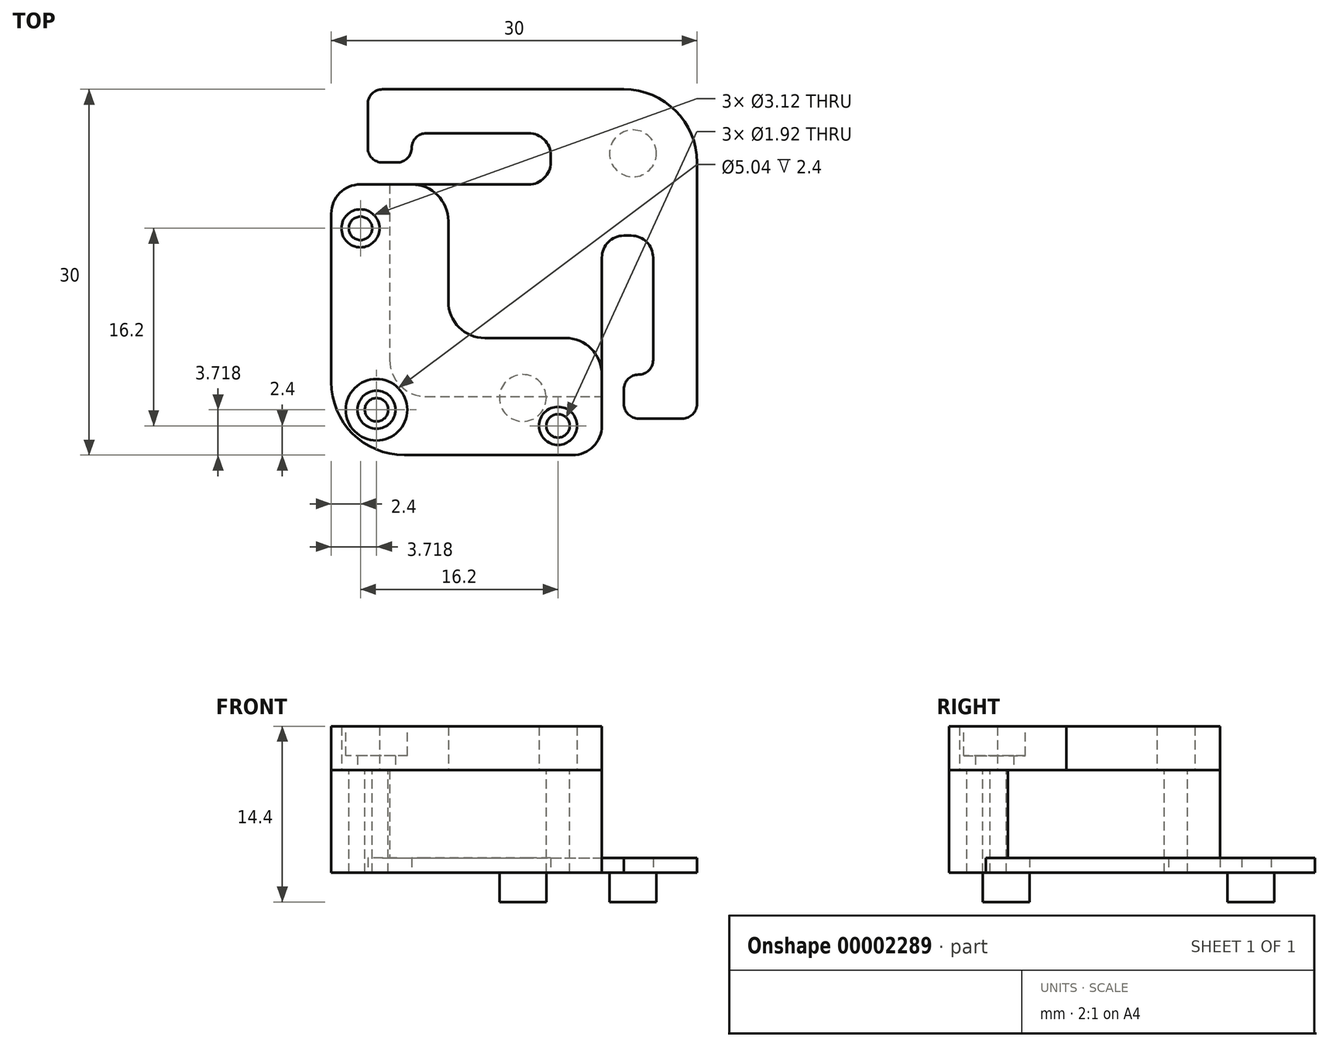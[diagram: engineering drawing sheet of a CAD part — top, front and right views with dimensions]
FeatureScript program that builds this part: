
annotation { "Feature Type Name" : "Feature", "Feature Type Description" : "" }
export const myFeature = defineFeature(function(context is Context, id is Id, definition is map)
    precondition{}
    {
        {
            var Q0;
            Q0=qCreatedBy(makeId("Top.planeOp"),FACE);
            var sketch = newSketch(context, id + "F0", { "sketchPlane" : qUnion([Q0])});
            skLineSegment(sketch, "E0.top", {"start": v(3.5, 25) * mm, "end": v(20, 25) * mm});
            skLineSegment(sketch, "E0.left", {"start": v(0, 5) * mm, "end": v(0, 16.5) * mm});
            skLineSegment(sketch, "E1", {"start": v(13.5, 22) * mm, "end": v(6.5, 22) * mm});
            skLineSegment(sketch, "E2", {"start": v(2, 18.5) * mm, "end": v(13.5, 18.5) * mm});
            skLineSegment(sketch, "E3", {"start": v(15, 20.5) * mm, "end": v(15, 20) * mm});
            skArc(sketch, "E4.filletArc", {"start": v(15, 20.5) * mm, "mid": v(14.56, 21.56) * mm, "end": v(13.5, 22) * mm});
            skArc(sketch, "E5.filletArc", {"start": v(13.5, 18.5) * mm, "mid": v(14.56, 18.94) * mm, "end": v(15, 20) * mm});
            skArc(sketch, "E6.filletArc", {"start": v(2, 18.5) * mm, "mid": v(0.59, 17.91) * mm, "end": v(0, 16.5) * mm});
            skPoint(sketch, "E7.visualSharp", {"position": v(0, 0) * mm});
            skLineSegment(sketch, "E8", {"start": v(5.5, 21) * mm, "end": v(5.5, 21) * mm});
            skLineSegment(sketch, "E9", {"start": v(4.5, 20) * mm, "end": v(3.5, 20) * mm});
            skLineSegment(sketch, "E10", {"start": v(2.5, 21) * mm, "end": v(2.5, 24) * mm});
            skPoint(sketch, "E11.visualSharp", {"position": v(5.5, 20) * mm});
            skArc(sketch, "E11.filletArc", {"start": v(4.5, 20) * mm, "mid": v(5.2, 20.3) * mm, "end": v(5.5, 21) * mm});
            skArc(sketch, "E12.filletArc", {"start": v(2.5, 21) * mm, "mid": v(2.8, 20.3) * mm, "end": v(3.5, 20) * mm});
            skArc(sketch, "E13.filletArc", {"start": v(6.5, 22) * mm, "mid": v(5.8, 21.7) * mm, "end": v(5.5, 21) * mm});
            skPoint(sketch, "E14.visualSharp", {"position": v(2.5, 25) * mm});
            skArc(sketch, "E14.filletArc", {"start": v(3.5, 25) * mm, "mid": v(2.8, 24.7) * mm, "end": v(2.5, 24) * mm});
            skLineSegment(sketch, "E15.bottom", {"start": v(0, 0) * mm, "end": v(25, 0) * mm, "construction": true});
            skLineSegment(sketch, "E15.top", {"start": v(0, 25) * mm, "end": v(25, 25) * mm, "construction": true});
            skLineSegment(sketch, "E15.left", {"start": v(0, 0) * mm, "end": v(0, 25) * mm, "construction": true});
            skLineSegment(sketch, "E15.right", {"start": v(25, 0) * mm, "end": v(25, 25) * mm, "construction": true});
            skLineSegment(sketch, "E16", {"start": v(0, 0) * mm, "end": v(25, 25) * mm, "construction": true});
            skLineSegment(sketch, "E17.0.MirrorCS", {"start": v(5, 0) * mm, "end": v(16.5, 0) * mm});
            skArc(sketch, "E18.0.MirrorCS", {"start": v(18.5, 2) * mm, "mid": v(17.91, 0.59) * mm, "end": v(16.5, 0) * mm});
            skLineSegment(sketch, "E19.0.MirrorCS", {"start": v(18.5, 2) * mm, "end": v(18.5, 13.5) * mm});
            skArc(sketch, "E20.0.MirrorCS", {"start": v(18.5, 13.5) * mm, "mid": v(18.94, 14.56) * mm, "end": v(20, 15) * mm});
            skLineSegment(sketch, "E21.0.MirrorCS", {"start": v(20.5, 15) * mm, "end": v(20, 15) * mm});
            skArc(sketch, "E22.0.MirrorCS", {"start": v(20.5, 15) * mm, "mid": v(21.56, 14.56) * mm, "end": v(22, 13.5) * mm});
            skLineSegment(sketch, "E23.0.MirrorCS", {"start": v(22, 13.5) * mm, "end": v(22, 6.5) * mm});
            skArc(sketch, "E24.0.MirrorCS", {"start": v(22, 6.5) * mm, "mid": v(21.7, 5.8) * mm, "end": v(21, 5.5) * mm});
            skArc(sketch, "E25.0.MirrorCS", {"start": v(20, 4.5) * mm, "mid": v(20.3, 5.2) * mm, "end": v(21, 5.5) * mm});
            skLineSegment(sketch, "E26.0.MirrorCS", {"start": v(20, 4.5) * mm, "end": v(20, 3.5) * mm});
            skArc(sketch, "E27.0.MirrorCS", {"start": v(21, 2.5) * mm, "mid": v(20.3, 2.8) * mm, "end": v(20, 3.5) * mm});
            skLineSegment(sketch, "E28.0.MirrorCS", {"start": v(21, 2.5) * mm, "end": v(24, 2.5) * mm});
            skArc(sketch, "E29.0.MirrorCS", {"start": v(25, 3.5) * mm, "mid": v(24.7, 2.8) * mm, "end": v(24, 2.5) * mm});
            skLineSegment(sketch, "E30.0.MirrorCS", {"start": v(25, 3.5) * mm, "end": v(25, 20) * mm});
            skArc(sketch, "E31.filletArc", {"start": v(0, 5) * mm, "mid": v(1.46, 1.46) * mm, "end": v(5, 0) * mm});
            skPoint(sketch, "E32.visualSharp", {"position": v(25, 25) * mm});
            skArc(sketch, "E32.filletArc", {"start": v(25, 20) * mm, "mid": v(23.54, 23.54) * mm, "end": v(20, 25) * mm});
            skSolve(sketch);
        }
        {
            var Q0;
            Q0=makeQuery(id+"F0.imprint","IMPRINT",FACE,{"disambiguationData":[TD([[makeQuery(id+"F0.imprint","IMPRINT",EDGE,{"derivedFrom":sQuery(id+"F0.wireOp",EDGE,"E0.bottom")}),1.0]])]});
            var Q1;
            Q1=makeQuery(id+"F0.imprint","IMPRINT",FACE,{"disambiguationData":[TD([[makeQuery(id+"F0.imprint","IMPRINT",EDGE,{"derivedFrom":sQuery(id+"F0.wireOp",EDGE,"E0.top")}),-1.0]])]});
            extrude(context, id + "F1", {"entities" : qUnion([Q0, Q1]), "depth" : 3 * mm});
        }
        {
            var Q0;
            Q0=makeQuery(id+"F1.opExtrude","CAP_FACE",FACE,{"disambiguationData":[OSD([sQuery(id+"F0.wireOp",EDGE,"E0.top"),sQuery(id+"F0.wireOp",EDGE,"E0.left"),sQuery(id+"F0.wireOp",EDGE,"E1"),sQuery(id+"F0.wireOp",EDGE,"E2"),sQuery(id+"F0.wireOp",EDGE,"E3"),sQuery(id+"F0.wireOp",EDGE,"E4.filletArc"),sQuery(id+"F0.wireOp",EDGE,"E5.filletArc"),sQuery(id+"F0.wireOp",EDGE,"E6.filletArc"),sQuery(id+"F0.wireOp",EDGE,"E9"),sQuery(id+"F0.wireOp",EDGE,"E10"),sQuery(id+"F0.wireOp",EDGE,"E11.filletArc"),sQuery(id+"F0.wireOp",EDGE,"E12.filletArc"),sQuery(id+"F0.wireOp",EDGE,"E13.filletArc"),sQuery(id+"F0.wireOp",EDGE,"E14.filletArc"),sQuery(id+"F0.wireOp",EDGE,"E17.0.MirrorCS"),sQuery(id+"F0.wireOp",EDGE,"E18.0.MirrorCS"),sQuery(id+"F0.wireOp",EDGE,"E19.0.MirrorCS"),sQuery(id+"F0.wireOp",EDGE,"E20.0.MirrorCS"),sQuery(id+"F0.wireOp",EDGE,"E21.0.MirrorCS"),sQuery(id+"F0.wireOp",EDGE,"E22.0.MirrorCS"),sQuery(id+"F0.wireOp",EDGE,"E23.0.MirrorCS"),sQuery(id+"F0.wireOp",EDGE,"E24.0.MirrorCS"),sQuery(id+"F0.wireOp",EDGE,"E25.0.MirrorCS"),sQuery(id+"F0.wireOp",EDGE,"E26.0.MirrorCS"),sQuery(id+"F0.wireOp",EDGE,"E27.0.MirrorCS"),sQuery(id+"F0.wireOp",EDGE,"E28.0.MirrorCS"),sQuery(id+"F0.wireOp",EDGE,"E29.0.MirrorCS"),sQuery(id+"F0.wireOp",EDGE,"E30.0.MirrorCS"),sQuery(id+"F0.wireOp",EDGE,"E31.filletArc"),sQuery(id+"F0.wireOp",EDGE,"E32.filletArc")])],"isStart":false});
            var sketch = newSketch(context, id + "F2", { "sketchPlane" : qUnion([Q0])});
            skLineSegment(sketch, "E33", {"start": v(0, 16.5) * mm, "end": v(0, 5) * mm});
            skLineSegment(sketch, "E34", {"start": v(5, 0) * mm, "end": v(16.5, 0) * mm});
            skLineSegment(sketch, "E35", {"start": v(4, 18.5) * mm, "end": v(4, 6.5) * mm});
            skLineSegment(sketch, "E36", {"start": v(6.5, 4) * mm, "end": v(18.5, 4) * mm});
            skLineSegment(sketch, "E37", {"start": v(2, 18.5) * mm, "end": v(4, 18.5) * mm});
            skLineSegment(sketch, "E38", {"start": v(18.5, 4) * mm, "end": v(18.5, 2) * mm});
            skArc(sketch, "E39", {"start": v(0, 5) * mm, "mid": v(1.46, 1.46) * mm, "end": v(5, 0) * mm});
            skArc(sketch, "E40", {"start": v(16.5, 0) * mm, "mid": v(17.91, 0.59) * mm, "end": v(18.5, 2) * mm});
            skArc(sketch, "E41", {"start": v(2, 18.5) * mm, "mid": v(0.59, 17.91) * mm, "end": v(0, 16.5) * mm});
            skPoint(sketch, "E42.visualSharp", {"position": v(4, 4) * mm});
            skArc(sketch, "E42.filletArc", {"start": v(4, 6.5) * mm, "mid": v(4.73, 4.73) * mm, "end": v(6.5, 4) * mm});
            skSolve(sketch);
        }
        {
            var Q0;
            Q0=makeQuery(id+"F2.imprint","IMPRINT",FACE,{"disambiguationData":[TD([[makeQuery(id+"F2.imprint","IMPRINT",EDGE,{"derivedFrom":sQuery(id+"F2.wireOp",EDGE,"E33")}),-1.0]])]});
            extrude(context, id + "F3", {"entities" : qUnion([Q0]), "operationType" : NewBodyOperationType.ADD, "depth" : 6 * mm});
        }
        {
            var Q0;
            Q0=makeQuery(id+"F3.opExtrude","CAP_FACE",FACE,{"disambiguationData":[OSD([sQuery(id+"F2.wireOp",EDGE,"E33"),sQuery(id+"F2.wireOp",EDGE,"E34"),sQuery(id+"F2.wireOp",EDGE,"E35"),sQuery(id+"F2.wireOp",EDGE,"E36"),sQuery(id+"F2.wireOp",EDGE,"E37"),sQuery(id+"F2.wireOp",EDGE,"E38"),sQuery(id+"F2.wireOp",EDGE,"E39"),sQuery(id+"F2.wireOp",EDGE,"E40"),sQuery(id+"F2.wireOp",EDGE,"E41"),sQuery(id+"F2.wireOp",EDGE,"E42.filletArc")])],"isStart":false});
            var sketch = newSketch(context, id + "F4", { "sketchPlane" : qUnion([Q0])});
            skLineSegment(sketch, "E43", {"start": v(0, 5) * mm, "end": v(0, 16.5) * mm});
            skLineSegment(sketch, "E44", {"start": v(2, 18.5) * mm, "end": v(5.5, 18.5) * mm});
            skLineSegment(sketch, "E45", {"start": v(8, 16) * mm, "end": v(8, 10.5) * mm});
            skLineSegment(sketch, "E46", {"start": v(10.5, 8) * mm, "end": v(16, 8) * mm});
            skLineSegment(sketch, "E47", {"start": v(18.5, 5.5) * mm, "end": v(18.5, 2) * mm});
            skLineSegment(sketch, "E48", {"start": v(5, 0) * mm, "end": v(16.5, 0) * mm});
            skArc(sketch, "E49", {"start": v(2, 18.5) * mm, "mid": v(0.59, 17.91) * mm, "end": v(0, 16.5) * mm});
            skArc(sketch, "E50", {"start": v(0, 5) * mm, "mid": v(1.46, 1.46) * mm, "end": v(5, 0) * mm});
            skArc(sketch, "E51", {"start": v(16.5, 0) * mm, "mid": v(17.91, 0.59) * mm, "end": v(18.5, 2) * mm});
            skPoint(sketch, "E52.visualSharp", {"position": v(8, 8) * mm});
            skArc(sketch, "E52.filletArc", {"start": v(8, 10.5) * mm, "mid": v(8.73, 8.73) * mm, "end": v(10.5, 8) * mm});
            skPoint(sketch, "E53.visualSharp", {"position": v(8, 18.5) * mm});
            skArc(sketch, "E53.filletArc", {"start": v(8, 16) * mm, "mid": v(7.27, 17.77) * mm, "end": v(5.5, 18.5) * mm});
            skPoint(sketch, "E54.visualSharp", {"position": v(18.5, 8) * mm});
            skArc(sketch, "E54.filletArc", {"start": v(18.5, 5.5) * mm, "mid": v(17.77, 7.27) * mm, "end": v(16, 8) * mm});
            skSolve(sketch);
        }
        {
            var Q0;
            {var subQ10=sQuery(id+"F4.wireOp",EDGE,"E45");Q0=qUnion([makeQuery(id+"F4.imprint","IMPRINT",FACE,{"disambiguationData":[TD([[makeQuery(id+"F4.imprint","IMPRINT",EDGE,{"derivedFrom":subQ10}),-1.0]])]}),makeQuery(id+"F4.imprint","IMPRINT",FACE,{"disambiguationData":[TD([[makeQuery(id+"F4.imprint","IMPRINT",EDGE,{"derivedFrom":sQuery(id+"F4.wireOp",EDGE,"E43")}),-1.0]])]})]);}
            extrude(context, id + "F5", {"entities" : qUnion([Q0]), "depth" : 3 * mm});
        }
        {
            var Q0;
            Q0=makeQuery(id+"F3.opExtrude","CAP_FACE",FACE,{"disambiguationData":[OSD([sQuery(id+"F2.wireOp",EDGE,"E33"),sQuery(id+"F2.wireOp",EDGE,"E34"),sQuery(id+"F2.wireOp",EDGE,"E35"),sQuery(id+"F2.wireOp",EDGE,"E36"),sQuery(id+"F2.wireOp",EDGE,"E37"),sQuery(id+"F2.wireOp",EDGE,"E38"),sQuery(id+"F2.wireOp",EDGE,"E39"),sQuery(id+"F2.wireOp",EDGE,"E40"),sQuery(id+"F2.wireOp",EDGE,"E41"),sQuery(id+"F2.wireOp",EDGE,"E42.filletArc")])],"isStart":false});
            var sketch = newSketch(context, id + "F6", { "sketchPlane" : qUnion([Q0])});
            skLineSegment(sketch, "E55", {"start": v(2, 18.57) * mm, "end": v(2, 2) * mm, "construction": true});
            skLineSegment(sketch, "E56", {"start": v(2, 2) * mm, "end": v(18.57, 2) * mm, "construction": true});
            skCircle(sketch, "E57", {"center": v(2, 15.5) * mm, "radius": 0.8 * mm});
            skCircle(sketch, "E58", {"center": v(3.1, 3.1) * mm, "radius": 0.8 * mm});
            skCircle(sketch, "E59", {"center": v(15.5, 2) * mm, "radius": 0.8 * mm});
            skLineSegment(sketch, "E60", {"start": v(1.46, 1.46) * mm, "end": v(4.73, 4.73) * mm, "construction": true});
            skCircle(sketch, "E61", {"center": v(2, 15.5) * mm, "radius": 1.3 * mm});
            skCircle(sketch, "E62", {"center": v(3.1, 3.1) * mm, "radius": 1.3 * mm});
            skCircle(sketch, "E63", {"center": v(15.5, 2) * mm, "radius": 1.3 * mm});
            skSolve(sketch);
        }
        {
            var Q0;
            Q0=makeQuery(id+"F6.imprint","IMPRINT",FACE,{"disambiguationData":[TD([[makeQuery(id+"F6.imprint","IMPRINT",EDGE,{"derivedFrom":sQuery(id+"F6.wireOp",EDGE,"E58")}),1.0]])]});
            var Q1;
            Q1=makeQuery(id+"F6.imprint","IMPRINT",FACE,{"disambiguationData":[TD([[makeQuery(id+"F6.imprint","IMPRINT",EDGE,{"derivedFrom":sQuery(id+"F6.wireOp",EDGE,"E57")}),1.0]])]});
            var Q2;
            Q2=makeQuery(id+"F6.imprint","IMPRINT",FACE,{"disambiguationData":[TD([[makeQuery(id+"F6.imprint","IMPRINT",EDGE,{"derivedFrom":sQuery(id+"F6.wireOp",EDGE,"E59")}),1.0]])]});
            extrude(context, id + "F7", {"entities" : qUnion([Q0, Q1, Q2]), "operationType" : NewBodyOperationType.REMOVE, "oppositeDirection" : true, "depth" : 25 * mm});
        }
        {
            var Q0;
            Q0=makeQuery(id+"F6.imprint","IMPRINT",FACE,{"disambiguationData":[TD([[makeQuery(id+"F6.imprint","IMPRINT",EDGE,{"derivedFrom":sQuery(id+"F6.wireOp",EDGE,"E58")}),-1.0]])]});
            var Q1;
            Q1=makeQuery(id+"F6.imprint","IMPRINT",FACE,{"disambiguationData":[TD([[makeQuery(id+"F6.imprint","IMPRINT",EDGE,{"derivedFrom":sQuery(id+"F6.wireOp",EDGE,"E58")}),1.0]])]});
            var Q2;
            Q2=makeQuery(id+"F6.imprint","IMPRINT",FACE,{"disambiguationData":[TD([[makeQuery(id+"F6.imprint","IMPRINT",EDGE,{"derivedFrom":sQuery(id+"F6.wireOp",EDGE,"E57")}),1.0]])]});
            var Q3;
            Q3=makeQuery(id+"F6.imprint","IMPRINT",FACE,{"disambiguationData":[TD([[makeQuery(id+"F6.imprint","IMPRINT",EDGE,{"derivedFrom":sQuery(id+"F6.wireOp",EDGE,"E57")}),-1.0]])]});
            var Q4;
            Q4=makeQuery(id+"F6.imprint","IMPRINT",FACE,{"disambiguationData":[TD([[makeQuery(id+"F6.imprint","IMPRINT",EDGE,{"derivedFrom":sQuery(id+"F6.wireOp",EDGE,"E59")}),1.0]])]});
            var Q5;
            Q5=makeQuery(id+"F6.imprint","IMPRINT",FACE,{"disambiguationData":[TD([[makeQuery(id+"F6.imprint","IMPRINT",EDGE,{"derivedFrom":sQuery(id+"F6.wireOp",EDGE,"E59")}),-1.0]])]});
            extrude(context, id + "F8", {"entities" : qUnion([Q0, Q1, Q2, Q3, Q4, Q5]), "operationType" : NewBodyOperationType.REMOVE, "depth" : 3 * mm});
        }
        {
            var Q0;
            Q0=makeQuery(id+"F5.opExtrude","CAP_FACE",FACE,{"disambiguationData":[OSD([sQuery(id+"F4.wireOp",EDGE,"E43"),sQuery(id+"F4.wireOp",EDGE,"E44"),sQuery(id+"F4.wireOp",EDGE,"E45"),sQuery(id+"F4.wireOp",EDGE,"E46"),sQuery(id+"F4.wireOp",EDGE,"E47"),sQuery(id+"F4.wireOp",EDGE,"E48"),sQuery(id+"F4.wireOp",EDGE,"E49"),sQuery(id+"F4.wireOp",EDGE,"E50"),sQuery(id+"F4.wireOp",EDGE,"E51"),sQuery(id+"F4.wireOp",EDGE,"E52.filletArc"),sQuery(id+"F4.wireOp",EDGE,"E53.filletArc"),sQuery(id+"F4.wireOp",EDGE,"E54.filletArc")])],"isStart":false});
            var sketch = newSketch(context, id + "F9", { "sketchPlane" : qUnion([Q0])});
            skCircle(sketch, "E64", {"center": v(2, 15.5) * mm, "radius": 2.1 * mm});
            skCircle(sketch, "E65", {"center": v(3.1, 3.1) * mm, "radius": 2.1 * mm});
            skCircle(sketch, "E66", {"center": v(15.5, 2) * mm, "radius": 2.1 * mm});
            skSolve(sketch);
        }
        {
            var Q0;
            Q0=makeQuery(id+"F9.imprint","IMPRINT",FACE,{"disambiguationData":[TD([[makeQuery(id+"F9.imprint","IMPRINT",EDGE,{"derivedFrom":makeQuery(id+"F8.boolean.opBoolean","COPY",EDGE,{"derivedFrom":makeQuery(id+"F8.opExtrude","CAP_EDGE",EDGE,{"disambiguationData":[OSD([sQuery(id+"F6.wireOp",EDGE,"E61")])],"isStart":false})})}),1.0]])]});
            var Q1;
            Q1=makeQuery(id+"F9.imprint","IMPRINT",FACE,{"disambiguationData":[TD([[makeQuery(id+"F9.imprint","IMPRINT",EDGE,{"derivedFrom":makeQuery(id+"F8.boolean.opBoolean","COPY",EDGE,{"derivedFrom":makeQuery(id+"F8.opExtrude","CAP_EDGE",EDGE,{"disambiguationData":[OSD([sQuery(id+"F6.wireOp",EDGE,"E62")])],"isStart":false})})}),1.0]])]});
            var Q2;
            Q2=makeQuery(id+"F9.imprint","IMPRINT",FACE,{"disambiguationData":[TD([[makeQuery(id+"F9.imprint","IMPRINT",EDGE,{"derivedFrom":makeQuery(id+"F8.boolean.opBoolean","COPY",EDGE,{"derivedFrom":makeQuery(id+"F8.opExtrude","CAP_EDGE",EDGE,{"disambiguationData":[OSD([sQuery(id+"F6.wireOp",EDGE,"E63")])],"isStart":false})})}),1.0]])]});
            var Q3;
            Q3=makeQuery(id+"F9.imprint","IMPRINT",FACE,{"disambiguationData":[TD([[makeQuery(id+"F9.imprint","IMPRINT",EDGE,{"derivedFrom":sQuery(id+"F9.wireOp",EDGE,"E65")}),1.0]])]});
            var Q4;
            Q4=makeQuery(id+"F9.imprint","IMPRINT",FACE,{"disambiguationData":[TD([[makeQuery(id+"F9.imprint","IMPRINT",EDGE,{"derivedFrom":sQuery(id+"F9.wireOp",EDGE,"E65")}),1.0]])]});
            var Q5;
            Q5=makeQuery(id+"F9.imprint","IMPRINT",FACE,{"disambiguationData":[TD([[makeQuery(id+"F9.imprint","IMPRINT",EDGE,{"derivedFrom":sQuery(id+"F9.wireOp",EDGE,"E64")}),1.0]])]});
            var Q6;
            Q6=makeQuery(id+"F9.imprint","IMPRINT",FACE,{"disambiguationData":[TD([[makeQuery(id+"F9.imprint","IMPRINT",EDGE,{"derivedFrom":sQuery(id+"F9.wireOp",EDGE,"E66")}),1.0]])]});
            var Q7;
            Q7=makeQuery(id+"F9.imprint","IMPRINT",FACE,{"disambiguationData":[TD([[makeQuery(id+"F9.imprint","IMPRINT",EDGE,{"derivedFrom":sQuery(id+"F9.wireOp",EDGE,"E66")}),1.0]])]});
            var Q8;
            Q8=makeQuery(id+"F9.imprint","IMPRINT",FACE,{"disambiguationData":[TD([[makeQuery(id+"F9.imprint","IMPRINT",EDGE,{"derivedFrom":sQuery(id+"F9.wireOp",EDGE,"E64")}),1.0]])]});
            var Q9;
            Q9=makeQuery(id+"F9.imprint","IMPRINT",FACE,{"disambiguationData":[TD([[makeQuery(id+"F9.imprint","IMPRINT",EDGE,{"derivedFrom":makeQuery(id+"F8.boolean.opBoolean","COPY",EDGE,{"derivedFrom":makeQuery(id+"F8.opExtrude","CAP_EDGE",EDGE,{"disambiguationData":[OSD([sQuery(id+"F6.wireOp",EDGE,"E61")])],"isStart":false})})}),-1.0]])]});
            var Q10;
            Q10=makeQuery(id+"F9.imprint","IMPRINT",FACE,{"disambiguationData":[TD([[makeQuery(id+"F9.imprint","IMPRINT",EDGE,{"derivedFrom":makeQuery(id+"F8.boolean.opBoolean","COPY",EDGE,{"derivedFrom":makeQuery(id+"F8.opExtrude","CAP_EDGE",EDGE,{"disambiguationData":[OSD([sQuery(id+"F6.wireOp",EDGE,"E63")])],"isStart":false})})}),-1.0]])]});
            extrude(context, id + "F10", {"entities" : qUnion([Q0, Q1, Q2, Q3, Q4, Q5, Q6, Q7, Q8, Q9, Q10]), "operationType" : NewBodyOperationType.REMOVE, "oppositeDirection" : true, "depth" : 2 * mm});
        }
        {
            var Q0;
            Q0=makeQuery(id+"F1.opExtrude","CAP_FACE",FACE,{"disambiguationData":[OSD([sQuery(id+"F0.wireOp",EDGE,"E0.top"),sQuery(id+"F0.wireOp",EDGE,"E0.left"),sQuery(id+"F0.wireOp",EDGE,"E1"),sQuery(id+"F0.wireOp",EDGE,"E2"),sQuery(id+"F0.wireOp",EDGE,"E3"),sQuery(id+"F0.wireOp",EDGE,"E4.filletArc"),sQuery(id+"F0.wireOp",EDGE,"E5.filletArc"),sQuery(id+"F0.wireOp",EDGE,"E6.filletArc"),sQuery(id+"F0.wireOp",EDGE,"E9"),sQuery(id+"F0.wireOp",EDGE,"E10"),sQuery(id+"F0.wireOp",EDGE,"E11.filletArc"),sQuery(id+"F0.wireOp",EDGE,"E12.filletArc"),sQuery(id+"F0.wireOp",EDGE,"E13.filletArc"),sQuery(id+"F0.wireOp",EDGE,"E14.filletArc"),sQuery(id+"F0.wireOp",EDGE,"E17.0.MirrorCS"),sQuery(id+"F0.wireOp",EDGE,"E18.0.MirrorCS"),sQuery(id+"F0.wireOp",EDGE,"E19.0.MirrorCS"),sQuery(id+"F0.wireOp",EDGE,"E20.0.MirrorCS"),sQuery(id+"F0.wireOp",EDGE,"E21.0.MirrorCS"),sQuery(id+"F0.wireOp",EDGE,"E22.0.MirrorCS"),sQuery(id+"F0.wireOp",EDGE,"E23.0.MirrorCS"),sQuery(id+"F0.wireOp",EDGE,"E24.0.MirrorCS"),sQuery(id+"F0.wireOp",EDGE,"E25.0.MirrorCS"),sQuery(id+"F0.wireOp",EDGE,"E26.0.MirrorCS"),sQuery(id+"F0.wireOp",EDGE,"E27.0.MirrorCS"),sQuery(id+"F0.wireOp",EDGE,"E28.0.MirrorCS"),sQuery(id+"F0.wireOp",EDGE,"E29.0.MirrorCS"),sQuery(id+"F0.wireOp",EDGE,"E30.0.MirrorCS"),sQuery(id+"F0.wireOp",EDGE,"E31.filletArc"),sQuery(id+"F0.wireOp",EDGE,"E32.filletArc")])],"isStart":true});
            var sketch = newSketch(context, id + "F11", { "sketchPlane" : qUnion([Q0])});
            skLineSegment(sketch, "E67", {"start": v(1.5, -15.5) * mm, "end": v(15.5, -1.5) * mm, "construction": true});
            skLineSegment(sketch, "E68", {"start": v(15.5, -1.5) * mm, "end": v(20.62, -20.62) * mm, "construction": true});
            skLineSegment(sketch, "E69", {"start": v(20.62, -20.62) * mm, "end": v(1.5, -15.5) * mm, "construction": true});
            skLineSegment(sketch, "E70", {"start": v(20.62, -20.62) * mm, "end": v(8.5, -8.5) * mm, "construction": true});
            skCircle(sketch, "E71", {"center": v(20.62, -20.62) * mm, "radius": 1.6 * mm});
            skCircle(sketch, "E72", {"center": v(3.9, -13.1) * mm, "radius": 1.6 * mm});
            skCircle(sketch, "E73.0.MirrorC", {"center": v(13.1, -3.9) * mm, "radius": 1.6 * mm});
            skSolve(sketch);
        }
        {
            var Q0;
            Q0=makeQuery(id+"F11.imprint","IMPRINT",FACE,{"disambiguationData":[TD([[makeQuery(id+"F11.imprint","IMPRINT",EDGE,{"derivedFrom":sQuery(id+"F11.wireOp",EDGE,"E72")}),1.0]])]});
            var Q1;
            Q1=makeQuery(id+"F11.imprint","IMPRINT",FACE,{"disambiguationData":[TD([[makeQuery(id+"F11.imprint","IMPRINT",EDGE,{"derivedFrom":sQuery(id+"F11.wireOp",EDGE,"E73.0.MirrorC")}),-1.0]])]});
            var Q2;
            Q2=makeQuery(id+"F11.imprint","IMPRINT",FACE,{"disambiguationData":[TD([[makeQuery(id+"F11.imprint","IMPRINT",EDGE,{"derivedFrom":sQuery(id+"F11.wireOp",EDGE,"E71")}),1.0]])]});
            extrude(context, id + "F12", {"entities" : qUnion([Q0, Q1, Q2]), "operationType" : NewBodyOperationType.REMOVE, "oppositeDirection" : true, "depth" : 2 * mm});
        }
        {
            var Q0;
            Q0=makeQuery(id+"F11.imprint","IMPRINT",FACE,{"disambiguationData":[TD([[makeQuery(id+"F11.imprint","IMPRINT",EDGE,{"derivedFrom":sQuery(id+"F11.wireOp",EDGE,"E71")}),1.0]])]});
            extrude(context, id + "F13", {"entities" : qUnion([Q0]), "oppositeDirection" : true, "depth" : 2 * mm});
        }
        {
            var Q0;
            Q0=makeQuery(id+"F1.opExtrude","SWEPT_BODY",BODY,{"disambiguationData":[OSD([sQuery(id+"F0.wireOp",EDGE,"E0.top"),sQuery(id+"F0.wireOp",EDGE,"E0.left"),sQuery(id+"F0.wireOp",EDGE,"E1"),sQuery(id+"F0.wireOp",EDGE,"E2"),sQuery(id+"F0.wireOp",EDGE,"E3"),sQuery(id+"F0.wireOp",EDGE,"E4.filletArc"),sQuery(id+"F0.wireOp",EDGE,"E5.filletArc"),sQuery(id+"F0.wireOp",EDGE,"E6.filletArc"),sQuery(id+"F0.wireOp",EDGE,"E9"),sQuery(id+"F0.wireOp",EDGE,"E10"),sQuery(id+"F0.wireOp",EDGE,"E11.filletArc"),sQuery(id+"F0.wireOp",EDGE,"E12.filletArc"),sQuery(id+"F0.wireOp",EDGE,"E13.filletArc"),sQuery(id+"F0.wireOp",EDGE,"E14.filletArc"),sQuery(id+"F0.wireOp",EDGE,"E17.0.MirrorCS"),sQuery(id+"F0.wireOp",EDGE,"E18.0.MirrorCS"),sQuery(id+"F0.wireOp",EDGE,"E19.0.MirrorCS"),sQuery(id+"F0.wireOp",EDGE,"E20.0.MirrorCS"),sQuery(id+"F0.wireOp",EDGE,"E21.0.MirrorCS"),sQuery(id+"F0.wireOp",EDGE,"E22.0.MirrorCS"),sQuery(id+"F0.wireOp",EDGE,"E23.0.MirrorCS"),sQuery(id+"F0.wireOp",EDGE,"E24.0.MirrorCS"),sQuery(id+"F0.wireOp",EDGE,"E25.0.MirrorCS"),sQuery(id+"F0.wireOp",EDGE,"E26.0.MirrorCS"),sQuery(id+"F0.wireOp",EDGE,"E27.0.MirrorCS"),sQuery(id+"F0.wireOp",EDGE,"E28.0.MirrorCS"),sQuery(id+"F0.wireOp",EDGE,"E29.0.MirrorCS"),sQuery(id+"F0.wireOp",EDGE,"E30.0.MirrorCS"),sQuery(id+"F0.wireOp",EDGE,"E31.filletArc"),sQuery(id+"F0.wireOp",EDGE,"E32.filletArc")])]});
            var Q1;
            Q1=makeQuery(id+"F5.opExtrude","SWEPT_BODY",BODY,{"disambiguationData":[OSD([sQuery(id+"F4.wireOp",EDGE,"E43"),sQuery(id+"F4.wireOp",EDGE,"E44"),sQuery(id+"F4.wireOp",EDGE,"E45"),sQuery(id+"F4.wireOp",EDGE,"E46"),sQuery(id+"F4.wireOp",EDGE,"E47"),sQuery(id+"F4.wireOp",EDGE,"E48"),sQuery(id+"F4.wireOp",EDGE,"E49"),sQuery(id+"F4.wireOp",EDGE,"E50"),sQuery(id+"F4.wireOp",EDGE,"E51"),sQuery(id+"F4.wireOp",EDGE,"E52.filletArc"),sQuery(id+"F4.wireOp",EDGE,"E53.filletArc"),sQuery(id+"F4.wireOp",EDGE,"E54.filletArc")])]});
            var Q2;
            Q2=makeQuery(id+"F13.opExtrude","SWEPT_BODY",BODY,{"disambiguationData":[OSD([sQuery(id+"F11.wireOp",EDGE,"E71")])]});
            var Q3;
            Q3=qCreatedBy(makeId("Origin.pointOp"),VERTEX);
            transform(context, id + "F14", {"entities" : qUnion([Q0, Q1, Q2]), "transformType" : TransformType.SCALE_UNIFORMLY, "scale" : 1.2, "makeCopy" : false, "scalePoint" : qUnion([Q3])});
        }
    });
